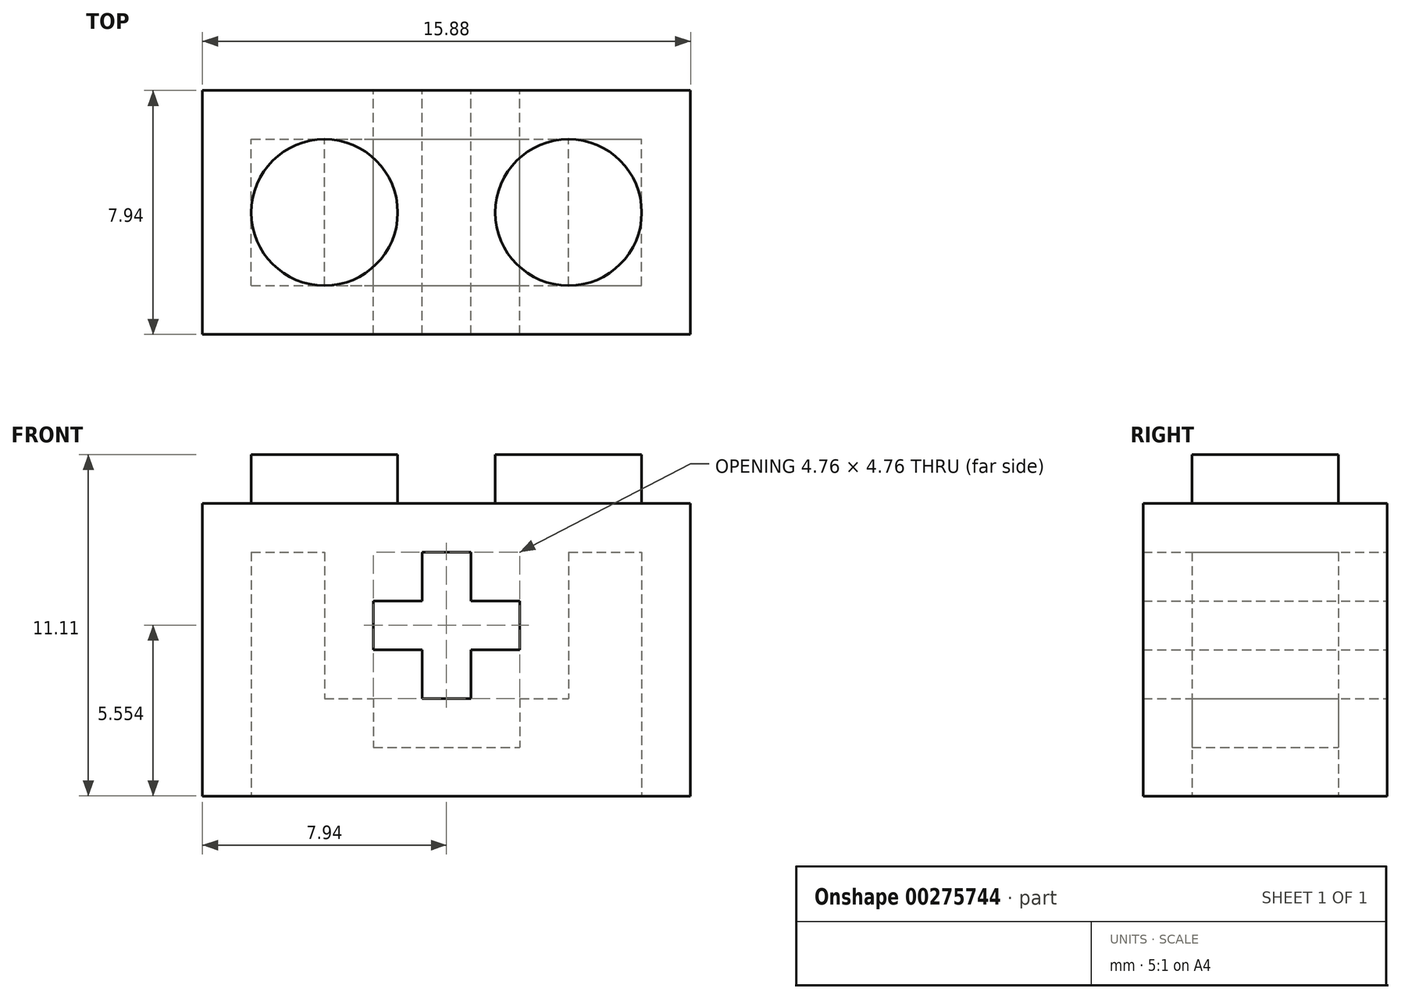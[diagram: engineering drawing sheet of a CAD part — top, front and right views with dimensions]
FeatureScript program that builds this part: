
annotation { "Feature Type Name" : "Feature", "Feature Type Description" : "" }
export const myFeature = defineFeature(function(context is Context, id is Id, definition is map)
    precondition{}
    {
        {
            var Q0;
            Q0=qCreatedBy(makeId("Front.planeOp"),FACE);
            var sketch = newSketch(context, id + "F0", { "sketchPlane" : qUnion([Q0])});
            skLineSegment(sketch, "E0.bottom", {"start": v(-7.94, 4.76) * mm, "end": v(7.94, 4.76) * mm});
            skLineSegment(sketch, "E0.top", {"start": v(-7.94, -4.76) * mm, "end": v(7.94, -4.76) * mm});
            skLineSegment(sketch, "E0.left", {"start": v(-7.94, 4.76) * mm, "end": v(-7.94, -4.76) * mm});
            skLineSegment(sketch, "E0.right", {"start": v(7.94, 4.76) * mm, "end": v(7.94, -4.76) * mm});
            skLineSegment(sketch, "E1.bottom", {"start": v(-0.8, 3.17) * mm, "end": v(0.8, 3.17) * mm});
            skLineSegment(sketch, "E1.top", {"start": v(-0.8, -1.59) * mm, "end": v(0.8, -1.59) * mm});
            skLineSegment(sketch, "E1.left", {"start": v(-0.8, 3.17) * mm, "end": v(-0.8, -1.59) * mm});
            skLineSegment(sketch, "E1.right", {"start": v(0.8, 3.17) * mm, "end": v(0.8, -1.59) * mm});
            skPoint(sketch, "E1.middle", {"position": v(0, 0) * mm});
            skLineSegment(sketch, "E2.bottom", {"start": v(-2.38, 1.59) * mm, "end": v(2.38, 1.59) * mm});
            skLineSegment(sketch, "E2.top", {"start": v(-2.38, 0) * mm, "end": v(2.38, 0) * mm});
            skLineSegment(sketch, "E2.left", {"start": v(-2.38, 1.59) * mm, "end": v(-2.38, 0) * mm});
            skLineSegment(sketch, "E2.right", {"start": v(2.38, 1.59) * mm, "end": v(2.38, 0) * mm});
            skLineSegment(sketch, "E3", {"start": v(-0.8, 3.17) * mm, "end": v(0.8, -1.59) * mm});
            skLineSegment(sketch, "E4", {"start": v(-2.38, 0) * mm, "end": v(2.38, 1.59) * mm});
            skSolve(sketch);
        }
        {
            var Q0;
            Q0=qSketchRegion(id+"F0",true);
            extrude(context, id + "F1", {"entities" : qUnion([Q0]), "depth" : 7.94 * mm});
        }
        {
            var Q0;
            Q0=makeQuery(id+"F1.opExtrude","SWEPT_FACE",FACE,{"disambiguationData":[OSD([sQuery(id+"F0.wireOp",EDGE,"E0.top")])]});
            shell(context, id + "F2", {"entities" : qUnion([Q0]), "thickness" : 1.59 * mm});
        }
        {
            var Q0;
            Q0=makeQuery(id+"F1.opExtrude","SWEPT_FACE",FACE,{"disambiguationData":[OSD([sQuery(id+"F0.wireOp",EDGE,"E0.bottom")])]});
            var sketch = newSketch(context, id + "F3", { "sketchPlane" : qUnion([Q0])});
            skCircle(sketch, "E5", {"center": v(-3.97, -3.97) * mm, "radius": 2.38 * mm});
            skCircle(sketch, "E6.1.0.0", {"center": v(3.97, -3.97) * mm, "radius": 2.38 * mm});
            skLineSegment(sketch, "E6.direction1", {"start": v(-3.97, -3.97) * mm, "end": v(3.97, -3.97) * mm, "construction": true});
            skSolve(sketch);
        }
        {
            var Q0;
            Q0=qSketchRegion(id+"F3",true);
            extrude(context, id + "F4", {"entities" : qUnion([Q0]), "operationType" : NewBodyOperationType.ADD, "depth" : 1.59 * mm});
        }
    });
